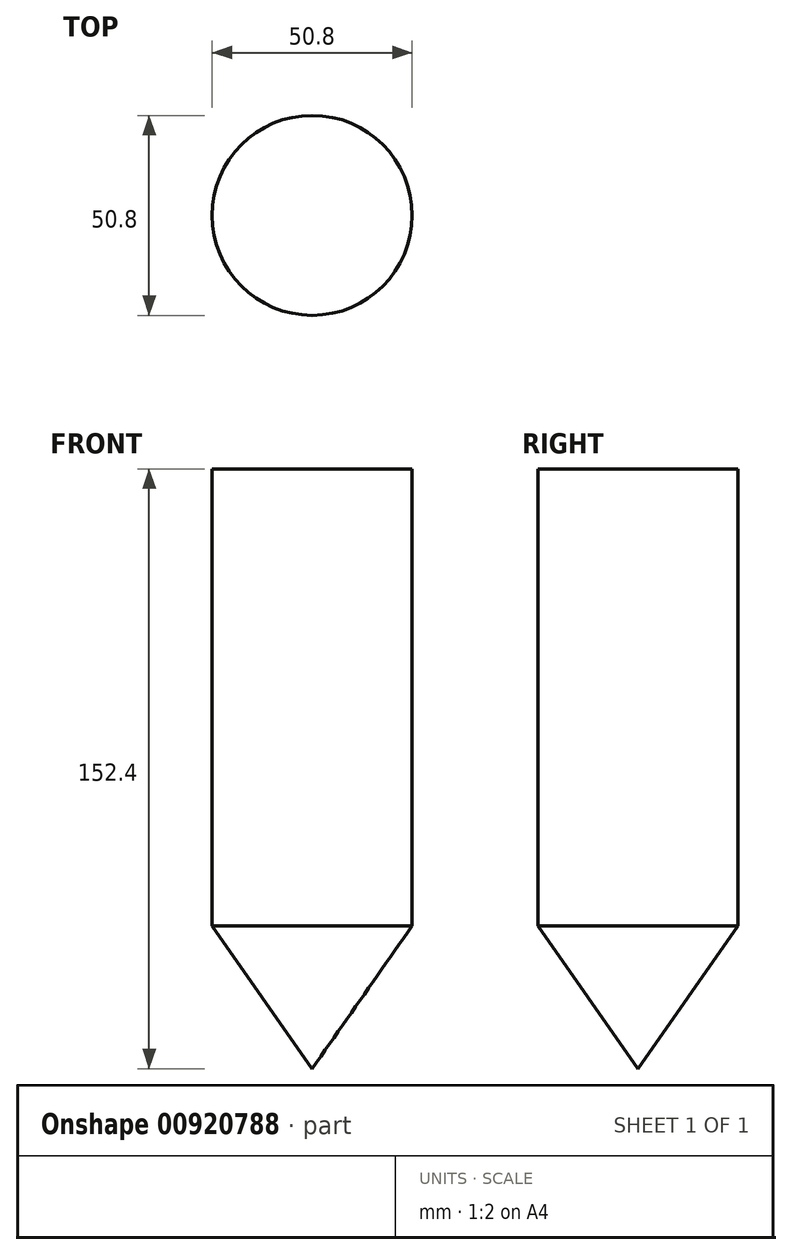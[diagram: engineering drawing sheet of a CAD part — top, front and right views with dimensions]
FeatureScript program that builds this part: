
annotation { "Feature Type Name" : "Feature", "Feature Type Description" : "" }
export const myFeature = defineFeature(function(context is Context, id is Id, definition is map)
    precondition{}
    {
        {
            var Q0;
            Q0=qCreatedBy(makeId("Front.planeOp"),FACE);
            var sketch = newSketch(context, id + "F0", { "sketchPlane" : qUnion([Q0])});
            skLineSegment(sketch, "E0", {"start": v(0, 0) * mm, "end": v(25.4, 0) * mm});
            skLineSegment(sketch, "E1", {"start": v(25.4, 0) * mm, "end": v(25.4, -116.13) * mm});
            skLineSegment(sketch, "E2", {"start": v(25.4, -116.13) * mm, "end": v(0, -152.4) * mm});
            skLineSegment(sketch, "E3", {"start": v(0, -152.4) * mm, "end": v(0, 0) * mm});
            skSolve(sketch);
        }
        {
            var Q0;
            Q0=makeQuery(id+"F0.imprint","IMPRINT",FACE,{"disambiguationData":[TD([[makeQuery(id+"F0.imprint","IMPRINT",EDGE,{"derivedFrom":sQuery(id+"F0.wireOp",EDGE,"E0")}),-1.0]])]});
            var Q1;
            Q1=sQuery(id+"F0.wireOp",EDGE,"E3");
            revolve(context, id + "F1", {"surfaceOperationType" : NewSurfaceOperationType.NEW, "entities" : qUnion([Q0]), "axis" : qUnion([Q1]), "revolveType" : RevolveType.FULL});
        }
    });
